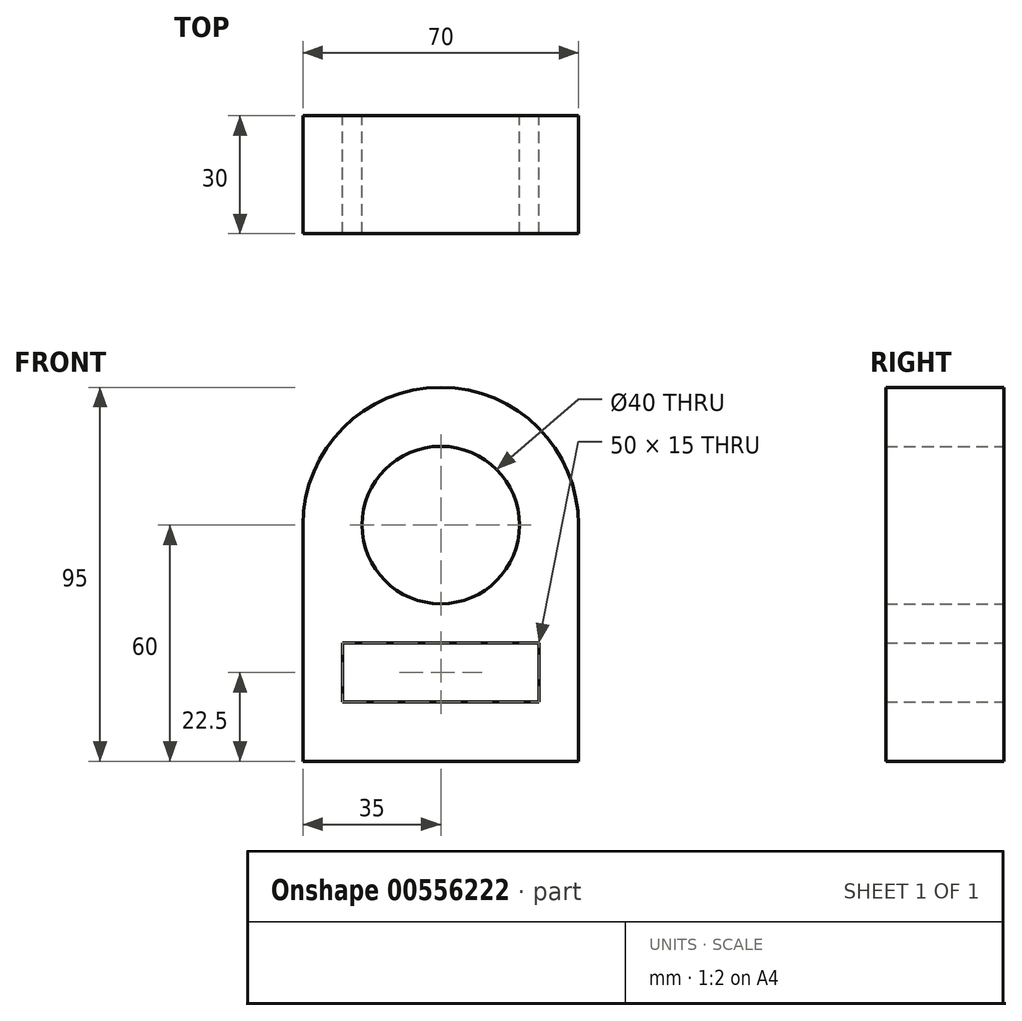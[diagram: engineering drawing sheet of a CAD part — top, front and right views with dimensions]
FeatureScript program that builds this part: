
annotation { "Feature Type Name" : "Feature", "Feature Type Description" : "" }
export const myFeature = defineFeature(function(context is Context, id is Id, definition is map)
    precondition{}
    {
        {
            var Q0;
            Q0=qCreatedBy(makeId("Front.planeOp"),FACE);
            var sketch = newSketch(context, id + "F0", { "sketchPlane" : qUnion([Q0])});
            skLineSegment(sketch, "E0", {"start": v(0, 0) * mm, "end": v(70, 0) * mm});
            skArc(sketch, "E1", {"start": v(70, 60) * mm, "mid": v(35, 95) * mm, "end": v(0, 60) * mm});
            skLineSegment(sketch, "E2", {"start": v(0, 0) * mm, "end": v(0, 60) * mm});
            skLineSegment(sketch, "E3", {"start": v(70, 0) * mm, "end": v(70, 60) * mm});
            skCircle(sketch, "E4", {"center": v(35, 60) * mm, "radius": 20 * mm});
            skLineSegment(sketch, "E5.bottom", {"start": v(10, 15) * mm, "end": v(60, 15) * mm});
            skLineSegment(sketch, "E5.top", {"start": v(10, 30) * mm, "end": v(60, 30) * mm});
            skLineSegment(sketch, "E5.left", {"start": v(10, 15) * mm, "end": v(10, 30) * mm});
            skLineSegment(sketch, "E5.right", {"start": v(60, 15) * mm, "end": v(60, 30) * mm});
            skSolve(sketch);
        }
        {
            var Q0;
            Q0 = qSketchRegion(id + "F0", true);
            extrude(context, id + "F1", {"entities" : qUnion([Q0]), "depth" : 30 * mm, "offsetDistance" : 25 * mm});
        }
    });
